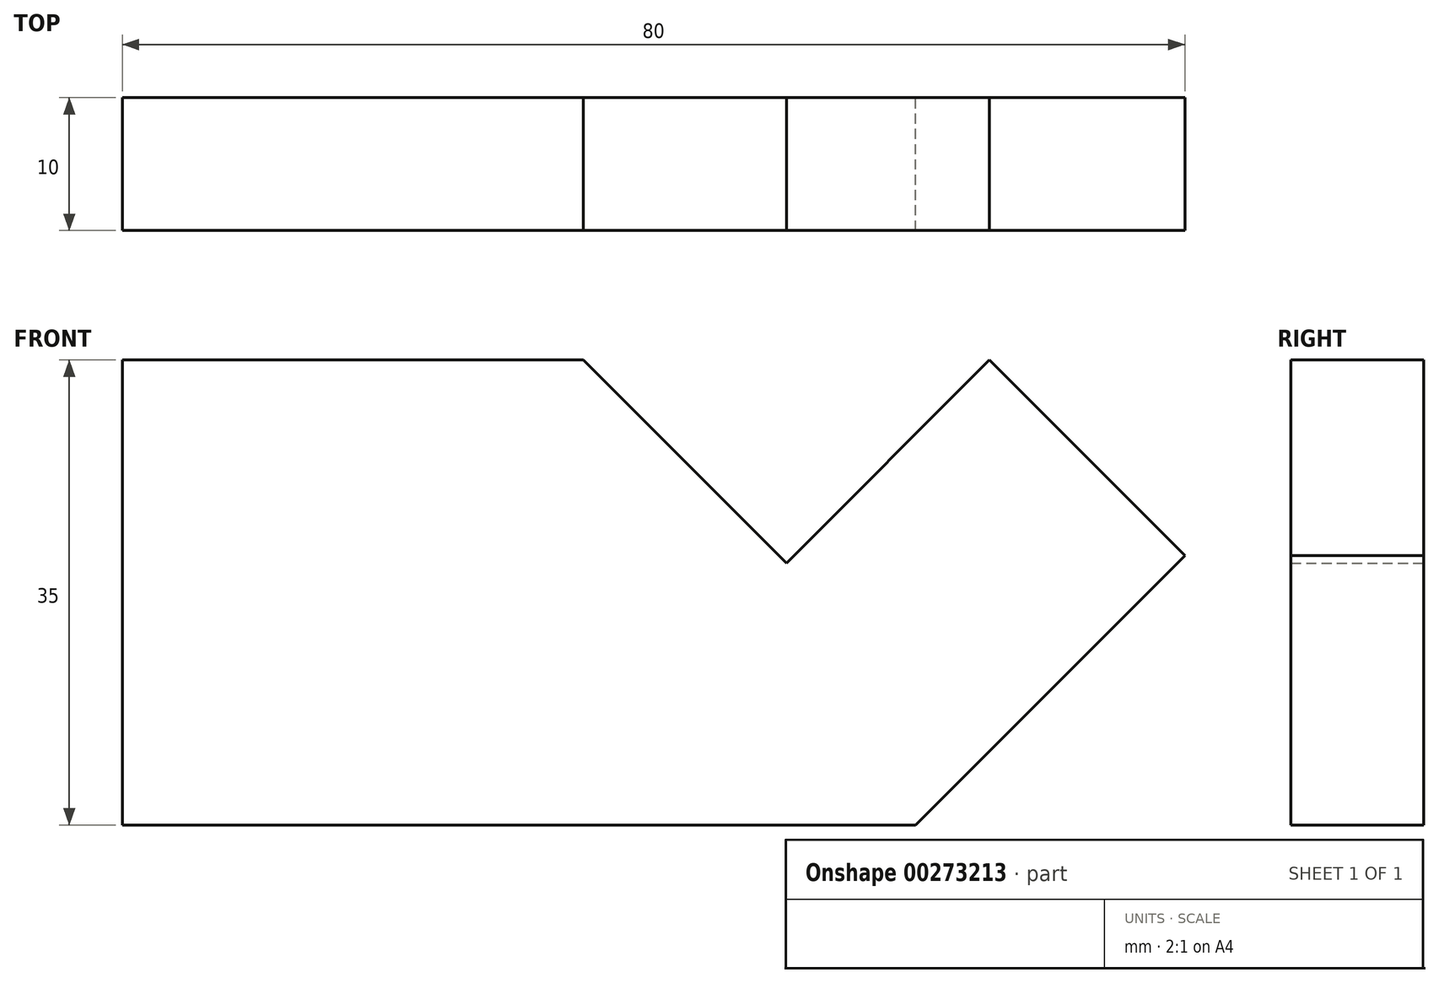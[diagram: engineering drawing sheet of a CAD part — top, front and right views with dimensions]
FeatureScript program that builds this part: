
annotation { "Feature Type Name" : "Feature", "Feature Type Description" : "" }
export const myFeature = defineFeature(function(context is Context, id is Id, definition is map)
    precondition{}
    {
        {
            var Q0;
            Q0=qCreatedBy(makeId("Front.planeOp"),FACE);
            var sketch = newSketch(context, id + "F0", { "sketchPlane" : qUnion([Q0])});
            skLineSegment(sketch, "E0", {"start": v(0, 0) * mm, "end": v(0, 35) * mm});
            skLineSegment(sketch, "E1", {"start": v(0, 35) * mm, "end": v(34.72, 35) * mm});
            skLineSegment(sketch, "E2", {"start": v(34.72, 35) * mm, "end": v(50, 19.72) * mm});
            skLineSegment(sketch, "E3", {"start": v(50, 19.72) * mm, "end": v(65.28, 35) * mm});
            skLineSegment(sketch, "E4", {"start": v(65.28, 35) * mm, "end": v(80, 20.28) * mm});
            skLineSegment(sketch, "E5", {"start": v(80, 20.28) * mm, "end": v(59.72, 0) * mm});
            skLineSegment(sketch, "E6", {"start": v(59.72, 0) * mm, "end": v(0, 0) * mm});
            skSolve(sketch);
        }
        {
            var Q0;
            Q0 = qSketchRegion(id + "F0", true);
            extrude(context, id + "F1", {"entities" : qUnion([Q0]), "depth" : 10 * mm});
        }
    });
